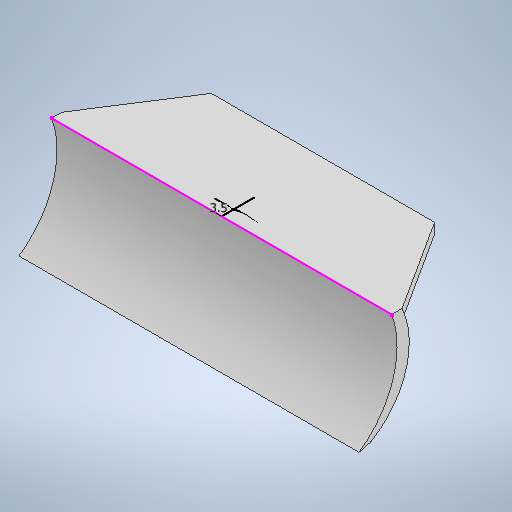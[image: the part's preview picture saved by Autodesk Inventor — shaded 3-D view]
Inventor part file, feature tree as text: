
AUTODESK INVENTOR PART (.ipt)
format: ipt  version: 2025.1 (Build 291241020, 241B)  size: 372,224 bytes
history: native  units: in
note: dims shown in document units (in); Inventor stores cm internally (conversion verified against a paired STEP export)
features: sketch x14, extrude x13
ambient origin geometry x8: Origin, YZ Plane, XZ Plane, XY Plane, X Axis, Y Axis, Z Axis, Center Point
bodies: Solid1 (feature_tree)
feature tree (27):
  extrude  "Extrusion1"  Depth=2.5591in
  extrude  "Extrusion2"  Depth=0.9843in TaperAngle=0.0deg
  extrude  "Extrusion3"  TaperAngle=165.0deg  [1 undecoded]
  extrude  "Extrusion4"  Depth=0.9843in TaperAngle=0.0deg
  sketch  "Sketch5"  dims[d12=0.4134in d13=0.2067in]
  extrude  "Extrusion5"  Depth=0.2067in
  extrude  "Extrusion6"  Depth=0.7382in
  sketch  "Sketch12"  dims[d16=0.7382in d17=0.1201in]
  extrude  "Extrusion12"  Depth=0.1201in
  extrude  "Extrusion13"  Depth=0.1201in
  extrude  "Extrusion14"  Depth=0.1181in
  extrude  "Extrusion15"  Depth=0.1181in
  extrude  "Extrusion16"  Depth=0.0984in TaperAngle=0.0deg
  sketch  "Sketch20"  dims[d60=0.3714in d62=0.139in]
  extrude  "Extrusion18"  Depth=0.7874in
  extrude  "Extrusion19"  Depth=0.139in
  sketch  "Sketch1"  dims[d0=1.2795in d1=2.5591in]
  sketch  "Sketch2"  dims[d2=0.748in d3=0.9843in d4=0.0in]
  sketch  "Sketch3"  dims[d5=0.4331in d6=165.0deg]
  sketch  "Sketch4"  dims[d7=0.9843in d8=0.0in d10=3.2062in d11=0.0in]
  sketch  "Sketch6"  dims[d14=0.5413in d15=0.7382in]
  sketch  "Sketch14"  dims[d18=0.1201in d19=0.1201in]
  sketch  "Sketch15"  dims[d20=0.1575in d21=0.0in d22=0.1181in]
  sketch  "Sketch16"  dims[d23=0.3937in d24=0.1181in]
  sketch  "Sketch17"  dims[d25=0.0984in d26=4.47in d27=0.0in]
  sketch  "Sketch18"  dims[d28=0.7874in d29=0.0in d59=1.1811in]
  sketch  "Sketch21"  dims[d63=15.0deg d64=0.3937in d65=0.0in d66=0.1181in d67=2.5591in d68=0.0in d69=0.1181in d70=0.6693in d71=0.0in d72=0.1181in d73=0.6693in d74=0.0in d75=2.6068in d76=0.0in d81=4.8937in d82=0.0in d83=4.8937in d84=0.0in d85=0.1378in d46=0.0197in d47=0.0344in d48=0.0197in d49=0.0344in d86=0.0344in]
note: 1 required parameter value undecoded (feature->parameter linkage not recoverable at this tier; creation-order binding heuristic only, values carry confidence <= 0.55)
